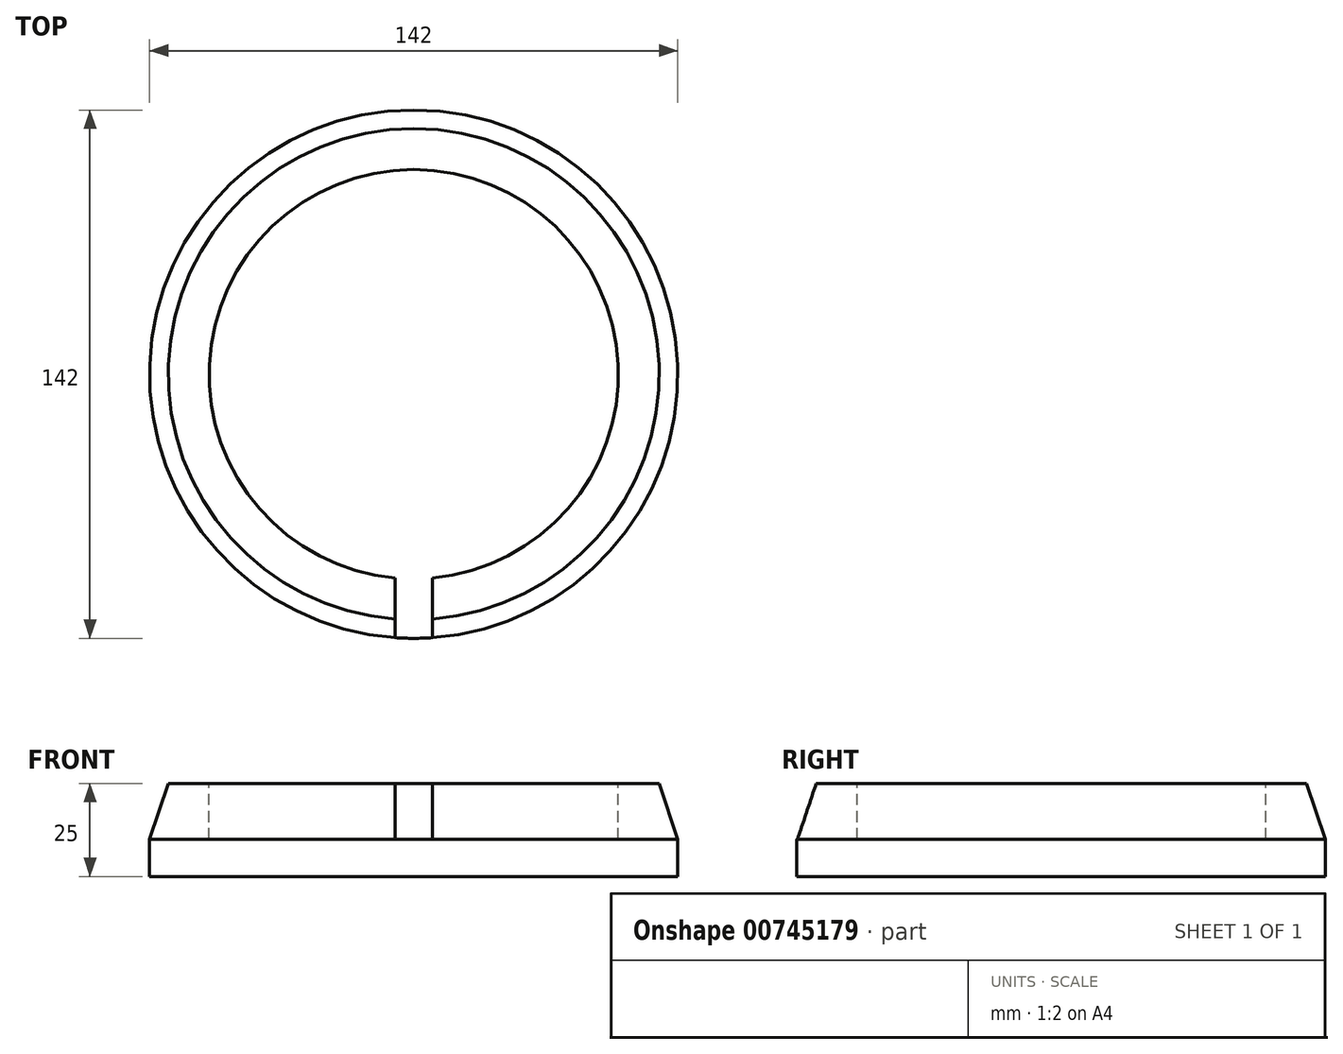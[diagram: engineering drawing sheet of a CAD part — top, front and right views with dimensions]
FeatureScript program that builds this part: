
annotation { "Feature Type Name" : "Feature", "Feature Type Description" : "" }
export const myFeature = defineFeature(function(context is Context, id is Id, definition is map)
    precondition{}
    {
        {
            var Q0;
            Q0=qCreatedBy(makeId("Top.planeOp"),FACE);
            var sketch = newSketch(context, id + "F0", { "sketchPlane" : qUnion([Q0])});
            skCircle(sketch, "E0", {"center": v(0, 0) * mm, "radius": 71 * mm});
            skSolve(sketch);
        }
        {
            var Q0;
            Q0 = qSketchRegion(id + "F0", true);
            extrude(context, id + "F1", {"entities" : qUnion([Q0]), "depth" : 25 * mm, "offsetDistance" : 25 * mm});
        }
        {
            var Q0;
            Q0=makeQuery(id+"F1.opExtrude","CAP_EDGE",EDGE,{"disambiguationData":[OSD([sQuery(id+"F0.wireOp",EDGE,"E0")])],"isStart":false});
            chamfer(context, id + "F2", {"entities" : qUnion([Q0]), "chamferType" : ChamferType.TWO_OFFSETS, "width1" : 5 * mm, "oppositeDirection" : false, "width2" : 15 * mm, "tangentPropagation" : true});
        }
        {
            var Q0;
            Q0=makeQuery(id+"F1.opExtrude","CAP_FACE",FACE,{"disambiguationData":[OSD([sQuery(id+"F0.wireOp",EDGE,"E0")])],"isStart":false});
            var sketch = newSketch(context, id + "F3", { "sketchPlane" : qUnion([Q0])});
            skCircle(sketch, "E1", {"center": v(0, 0) * mm, "radius": 55 * mm});
            skSolve(sketch);
        }
        {
            var Q0;
            Q0 = qSketchRegion(id + "F3", true);
            extrude(context, id + "F4", {"entities" : qUnion([Q0]), "operationType" : NewBodyOperationType.REMOVE, "oppositeDirection" : true, "depth" : 15 * mm, "offsetDistance" : 25 * mm});
        }
        {
            var Q0;
            Q0=qCreatedBy(makeId("Front.planeOp"),FACE);
            var sketch = newSketch(context, id + "F5", { "sketchPlane" : qUnion([Q0])});
            skLineSegment(sketch, "E2.bottom", {"start": v(-5, 30) * mm, "end": v(5, 30) * mm});
            skLineSegment(sketch, "E2.top", {"start": v(-5, 10) * mm, "end": v(5, 10) * mm});
            skLineSegment(sketch, "E2.left", {"start": v(-5, 30) * mm, "end": v(-5, 10) * mm});
            skLineSegment(sketch, "E2.right", {"start": v(5, 30) * mm, "end": v(5, 10) * mm});
            skSolve(sketch);
        }
        {
            var Q0;
            Q0 = qSketchRegion(id + "F5", true);
            extrude(context, id + "F6", {"entities" : qUnion([Q0]), "operationType" : NewBodyOperationType.REMOVE, "depth" : 114.4 * mm, "offsetDistance" : 25 * mm});
        }
        {
            var Q0;
            Q0=qCreatedBy(makeId("Front.planeOp"),FACE);
            var sketch = newSketch(context, id + "F7", { "sketchPlane" : qUnion([Q0])});
            skLineSegment(sketch, "E3", {"start": v(0, -26.5) * mm, "end": v(0, 42.14) * mm, "construction": true});
            skSolve(sketch);
        }
    });
